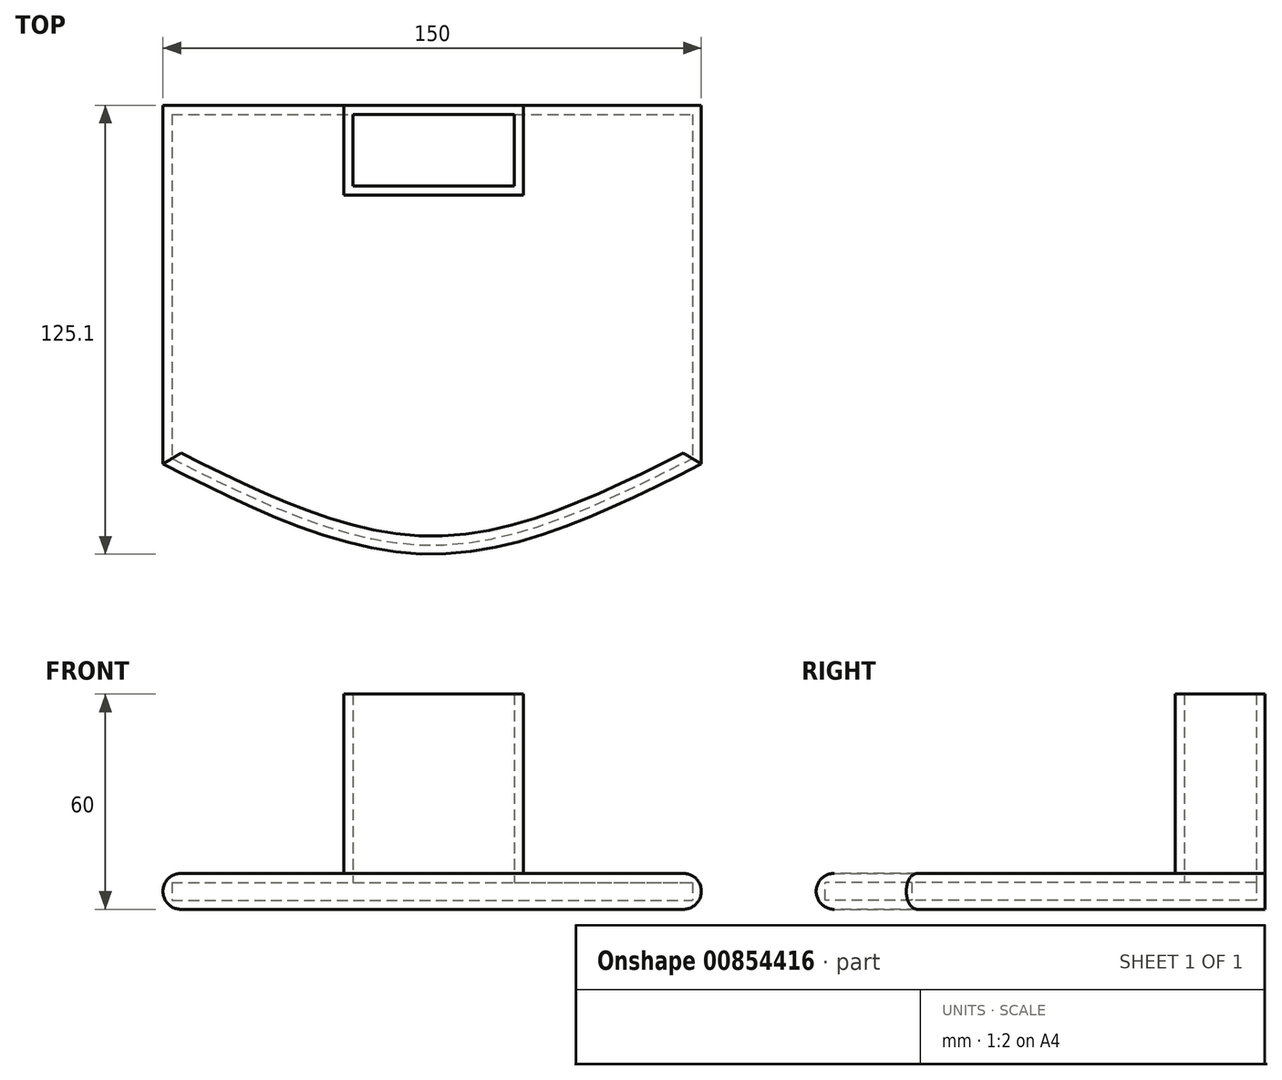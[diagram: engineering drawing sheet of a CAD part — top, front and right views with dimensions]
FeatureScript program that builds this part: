
annotation { "Feature Type Name" : "Feature", "Feature Type Description" : "" }
export const myFeature = defineFeature(function(context is Context, id is Id, definition is map)
    precondition{}
    {
        {
            var Q0;
            Q0=qCreatedBy(makeId("Top.planeOp"),FACE);
            var sketch = newSketch(context, id + "F0", { "sketchPlane" : qUnion([Q0])});
            skLineSegment(sketch, "E0.bottom", {"start": v(-75, 50) * mm, "end": v(75, 50) * mm});
            skLineSegment(sketch, "E0.left", {"start": v(-75, 50) * mm, "end": v(-75, -50) * mm});
            skLineSegment(sketch, "E0.right", {"start": v(75, 50) * mm, "end": v(75, -50) * mm});
            skFitSpline(sketch, "E1", {"points": [v(-75, -50) * mm, v(0, -75.1) * mm, v(75, -50) * mm], "startDerivative": vector(150, -75.3) * mm, "endDerivative": vector(150, 75.3) * mm});
            skSolve(sketch);
        }
        {
            var Q0;
            Q0=makeQuery(id+"F0.imprint","IMPRINT",FACE,{"disambiguationData":[TD([[makeQuery(id+"F0.imprint","IMPRINT",EDGE,{"derivedFrom":sQuery(id+"F0.wireOp",EDGE,"E0.bottom")}),-1.0]])]});
            extrude(context, id + "F1", {"entities" : qUnion([Q0]), "depth" : 10 * mm, "offsetDistance" : 25 * mm});
        }
        {
            var Q0;
            Q0=makeQuery(id+"F1.opExtrude","CAP_FACE",FACE,{"disambiguationData":[OSD([sQuery(id+"F0.wireOp",EDGE,"E0.bottom"),sQuery(id+"F0.wireOp",EDGE,"E0.left"),sQuery(id+"F0.wireOp",EDGE,"E0.right"),sQuery(id+"F0.wireOp",EDGE,"E1")])],"isStart":false});
            var sketch = newSketch(context, id + "F2", { "sketchPlane" : qUnion([Q0])});
            skLineSegment(sketch, "E2.bottom", {"start": v(-24.55, 50) * mm, "end": v(25.45, 50) * mm});
            skLineSegment(sketch, "E2.top", {"start": v(-24.55, 25) * mm, "end": v(25.45, 25) * mm});
            skLineSegment(sketch, "E2.left", {"start": v(-24.55, 50) * mm, "end": v(-24.55, 25) * mm});
            skLineSegment(sketch, "E2.right", {"start": v(25.45, 50) * mm, "end": v(25.45, 25) * mm});
            skSolve(sketch);
        }
        {
            var Q0;
            Q0=makeQuery(id+"F2.imprint","IMPRINT",FACE,{"disambiguationData":[TD([[makeQuery(id+"F2.imprint","IMPRINT",EDGE,{"derivedFrom":sQuery(id+"F2.wireOp",EDGE,"E2.bottom")}),-1.0]])]});
            extrude(context, id + "F3", {"entities" : qUnion([Q0]), "operationType" : NewBodyOperationType.ADD, "depth" : 50 * mm, "offsetDistance" : 25 * mm});
        }
        {
            var Q0;
            Q0=makeQuery(id+"F3.opExtrude","CAP_FACE",FACE,{"disambiguationData":[OSD([sQuery(id+"F2.wireOp",EDGE,"E2.bottom"),sQuery(id+"F2.wireOp",EDGE,"E2.top"),sQuery(id+"F2.wireOp",EDGE,"E2.left"),sQuery(id+"F2.wireOp",EDGE,"E2.right")])],"isStart":false});
            shell(context, id + "F4", {"entities" : qUnion([Q0]), "thickness" : 2.5 * mm});
        }
        {
            var Q0;
            Q0=makeQuery(id+"F1.opExtrude","CAP_EDGE",EDGE,{"disambiguationData":[OSD([sQuery(id+"F0.wireOp",EDGE,"E1")])],"isStart":false});
            var Q1;
            Q1=makeQuery(id+"F1.opExtrude","CAP_EDGE",EDGE,{"disambiguationData":[OSD([sQuery(id+"F0.wireOp",EDGE,"E1")])],"isStart":true});
            var Q2;
            Q2=makeQuery(id+"F1.opExtrude","CAP_EDGE",EDGE,{"disambiguationData":[OSD([sQuery(id+"F0.wireOp",EDGE,"E0.left")])],"isStart":false});
            var Q3;
            Q3=makeQuery(id+"F1.opExtrude","CAP_EDGE",EDGE,{"disambiguationData":[OSD([sQuery(id+"F0.wireOp",EDGE,"E0.left")])],"isStart":true});
            var Q4;
            Q4=makeQuery(id+"F1.opExtrude","CAP_EDGE",EDGE,{"disambiguationData":[OSD([sQuery(id+"F0.wireOp",EDGE,"E0.right")])],"isStart":true});
            var Q5;
            Q5=makeQuery(id+"F1.opExtrude","CAP_EDGE",EDGE,{"disambiguationData":[OSD([sQuery(id+"F0.wireOp",EDGE,"E0.right")])],"isStart":false});
            var Q6;
            Q6=makeQuery(id+"F3.opExtrude","CAP_EDGE",EDGE,{"disambiguationData":[OSD([sQuery(id+"F2.wireOp",EDGE,"E2.top")])],"isStart":true});
            fillet(context, id + "F5", {"entities" : qUnion([Q0, Q1, Q2, Q3, Q4, Q5, Q6]), "radius" : 5 * mm, "tangentPropagation" : true, "allowEdgeOverflow" : false});
        }
    });
